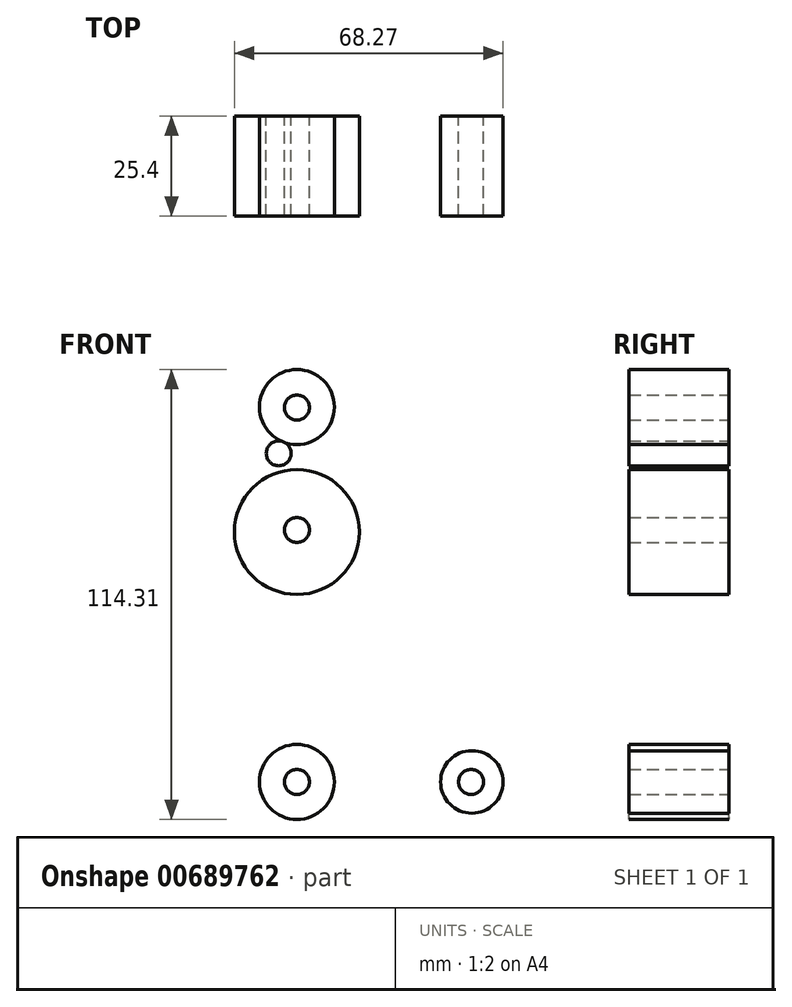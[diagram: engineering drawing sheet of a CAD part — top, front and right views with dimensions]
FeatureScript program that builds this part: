
annotation { "Feature Type Name" : "Feature", "Feature Type Description" : "" }
export const myFeature = defineFeature(function(context is Context, id is Id, definition is map)
    precondition{}
    {
        {
            var Q0;
            Q0=qCreatedBy(makeId("Front.planeOp"),FACE);
            var sketch = newSketch(context, id + "F0", { "sketchPlane" : qUnion([Q0])});
            skLineSegment(sketch, "E0", {"start": v(0, 0) * mm, "end": v(44.45, 0) * mm});
            skCircle(sketch, "E1", {"center": v(0, 95.25) * mm, "radius": 9.53 * mm});
            skCircle(sketch, "E2", {"center": v(0, 63.5) * mm, "radius": 15.88 * mm});
            skCircle(sketch, "E3", {"center": v(0, 0) * mm, "radius": 9.53 * mm});
            skCircle(sketch, "E4", {"center": v(44.45, 0) * mm, "radius": 7.94 * mm});
            skLineSegment(sketch, "E5", {"start": v(0, 0) * mm, "end": v(0, 63.5) * mm, "construction": true});
            skLineSegment(sketch, "E6", {"start": v(0, 63.5) * mm, "end": v(0, 95.25) * mm, "construction": true});
            skSolve(sketch);
        }
        {
            var Q0;
            Q0=qCreatedBy(makeId("Front.planeOp"),FACE);
            var sketch = newSketch(context, id + "F1", { "sketchPlane" : qUnion([Q0])});
            skLineSegment(sketch, "E7", {"start": v(-9.63, 95.7) * mm, "end": v(-16.04, 64.31) * mm});
            skLineSegment(sketch, "E8", {"start": v(-16.04, 64.31) * mm, "end": v(-9.57, 0) * mm});
            skLineSegment(sketch, "E9", {"start": v(9.39, 96.89) * mm, "end": v(16.04, 64.31) * mm});
            skLineSegment(sketch, "E10", {"start": v(18.97, 8.85) * mm, "end": v(45.28, 7.91) * mm});
            skLineSegment(sketch, "E11", {"start": v(0, -9.53) * mm, "end": v(47.77, -7.82) * mm});
            skLineSegment(sketch, "E12", {"start": v(16.04, 64.31) * mm, "end": v(11.34, 17.6) * mm});
            skCircle(sketch, "E13", {"center": v(0, 95.12) * mm, "radius": 3.18 * mm});
            skCircle(sketch, "E14", {"center": v(0, 64.01) * mm, "radius": 3.18 * mm});
            skCircle(sketch, "E15", {"center": v(0, 0) * mm, "radius": 3.18 * mm});
            skCircle(sketch, "E16", {"center": v(44.26, 0) * mm, "radius": 3.18 * mm});
            skPoint(sketch, "E17.newPointA", {"position": v(9.57, 0) * mm});
            skPoint(sketch, "E17.newPointB", {"position": v(0, 9.53) * mm});
            skArc(sketch, "E17.filletArc", {"start": v(11.34, 17.6) * mm, "mid": v(13.26, 11.57) * mm, "end": v(18.97, 8.85) * mm});
            skCircle(sketch, "E18", {"center": v(-4.61, 83.5) * mm, "radius": 3.18 * mm});
            skSolve(sketch);
        }
        {
            var Q0;
            Q0 = qSketchRegion(id + "F0", true);
            var Q1;
            Q1 = qSketchRegion(id + "F1", true);
            extrude(context, id + "F2", {"entities" : qUnion([Q0, Q1]), "depth" : 25.4 * mm, "offsetDistance" : 25.4 * mm});
        }
    });
